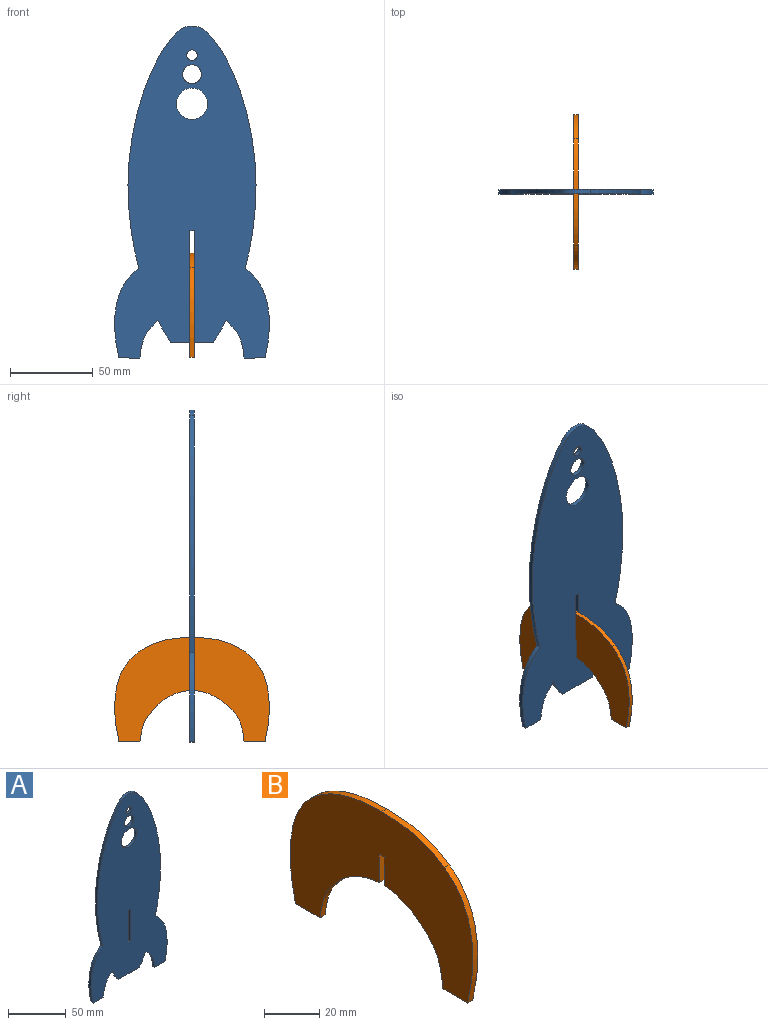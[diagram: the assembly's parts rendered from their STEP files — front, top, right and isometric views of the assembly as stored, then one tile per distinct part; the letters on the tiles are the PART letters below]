
ASSEMBLY  parts=2 mates=1
PART A: 21 faces, bbox 95.3x2.5x200.4 mm
  f0: plane 200.4x95.26mm, normal (0,-1,0), area 12643mm2, adj f2,f3,f4,f5,f6,f7,f8,f9
  f1: plane 200.4x95.26mm, normal (0,1,0), area 12643mm2, adj f2,f3,f4,f5,f6,f7,f8,f9
  f2: extruded ~142.79x29.78mm, area 381.3mm2, adj f0,f1,f3,f13
  f3: extruded ~53.99x14.65mm, area 149.4mm2, adj f0,f1,f2,f4
  f4: plane 12.7x2.54mm, normal (0,0,-1), area 32.3mm2, adj f0,f1,f3,f5
  f5: extruded ~22.58x10.85mm, area 65.9mm2, adj f0,f1,f4,f6
  f6: extruded ~13.05x7.86mm, area 38.8mm2, adj f0,f1,f5,f7
  f7: plane 25.4x2.54mm, normal (0,0,-1), area 64.5mm2, adj f0,f1,f6,f8
  f8: extruded ~13.05x7.86mm, area 38.8mm2, adj f0,f1,f7,f9
  f9: extruded ~22.58x10.85mm, area 65.9mm2, adj f0,f1,f8,f10
  f10: plane 12.7x2.54mm, normal (0,0,-1), area 32.3mm2, adj f0,f1,f9,f11
  f11: extruded ~53.99x14.65mm, area 149.4mm2, adj f0,f1,f10,f12
  f12: extruded ~142.79x29.78mm, area 381.3mm2, adj f0,f1,f11,f13
  f13: cylinder r=12.7mm len=17.75mm, axis (0,1,0), area 49.9mm2, adj f0,f1,f2,f12
  f14: plane 33.37x2.54mm, normal (-1,0,0), area 84.8mm2, adj f0,f1,f16,f17
  f15: plane 33.37x2.54mm, normal (1,0,0), area 84.8mm2, adj f0,f1,f16,f17
  f16: plane 2.54x2.54mm, normal (0,0,1), area 6.5mm2, adj f0,f1,f14,f15
  f17: plane 2.54x2.54mm, normal (0,0,-1), area 6.5mm2, adj f0,f1,f14,f15
  f18: cylinder r=3.17mm len=6.35mm, axis (0,1,0), area 50.7mm2, adj f0,f1
  f19: cylinder r=5.66mm len=11.33mm, axis (0,1,0), area 90.4mm2, adj f0,f1
  f20: cylinder r=9.53mm len=19.05mm, axis (0,1,0), area 152mm2, adj f0,f1
PART B: 15 faces, bbox 2.5x95.3x62.8 mm
  f0: extruded ~19.29x8.06mm, area 54.1mm2, adj f1,f6,f11,f13
  f1: plane 95.26x62.78mm, normal (1,0,0), area 3628.3mm2, adj f0,f2,f3,f4,f5,f6,f7,f8
  f2: extruded ~32.09x8.78mm, area 86mm2, adj f1,f3,f10,f11
  f3: extruded ~32.09x8.78mm, area 86mm2, adj f1,f2,f4,f11
  f4: extruded ~53.99x14.65mm, area 149.4mm2, adj f1,f3,f5,f11
  f5: plane 12.7x2.54mm, normal (0,0,-1), area 32.3mm2, adj f1,f4,f6,f11
  f6: extruded ~22.58x10.85mm, area 65.3mm2, adj f0,f1,f5,f11
  f7: extruded ~19.29x8.06mm, area 54.1mm2, adj f1,f8,f11,f12
  f8: extruded ~22.58x10.85mm, area 65.9mm2, adj f1,f7,f9,f11
  f9: plane 12.7x2.54mm, normal (0,0,-1), area 32.3mm2, adj f1,f8,f10,f11
  f10: extruded ~53.99x14.65mm, area 149.4mm2, adj f1,f2,f9,f11
  f11: plane 95.26x62.78mm, normal (-1,0,0), area 3628.3mm2, adj f0,f2,f3,f4,f5,f6,f7,f8
  f12: plane 12.73x2.54mm, normal (0,1,0), area 32.3mm2, adj f1,f7,f11,f14
  f13: plane 12.73x2.54mm, normal (0,-1,0), area 32.3mm2, adj f0,f1,f11,f14
  f14: plane 2.54x2.54mm, normal (0,0,-1), area 6.5mm2, adj f1,f11,f12,f13
PLACE A t=(0,0,-76.74)mm
PLACE B t=(0,0,-76.39)mm
MATE slider B.f14 <-> A.f17  axis (0,0,-1) through (0,0,-33.02)mm
